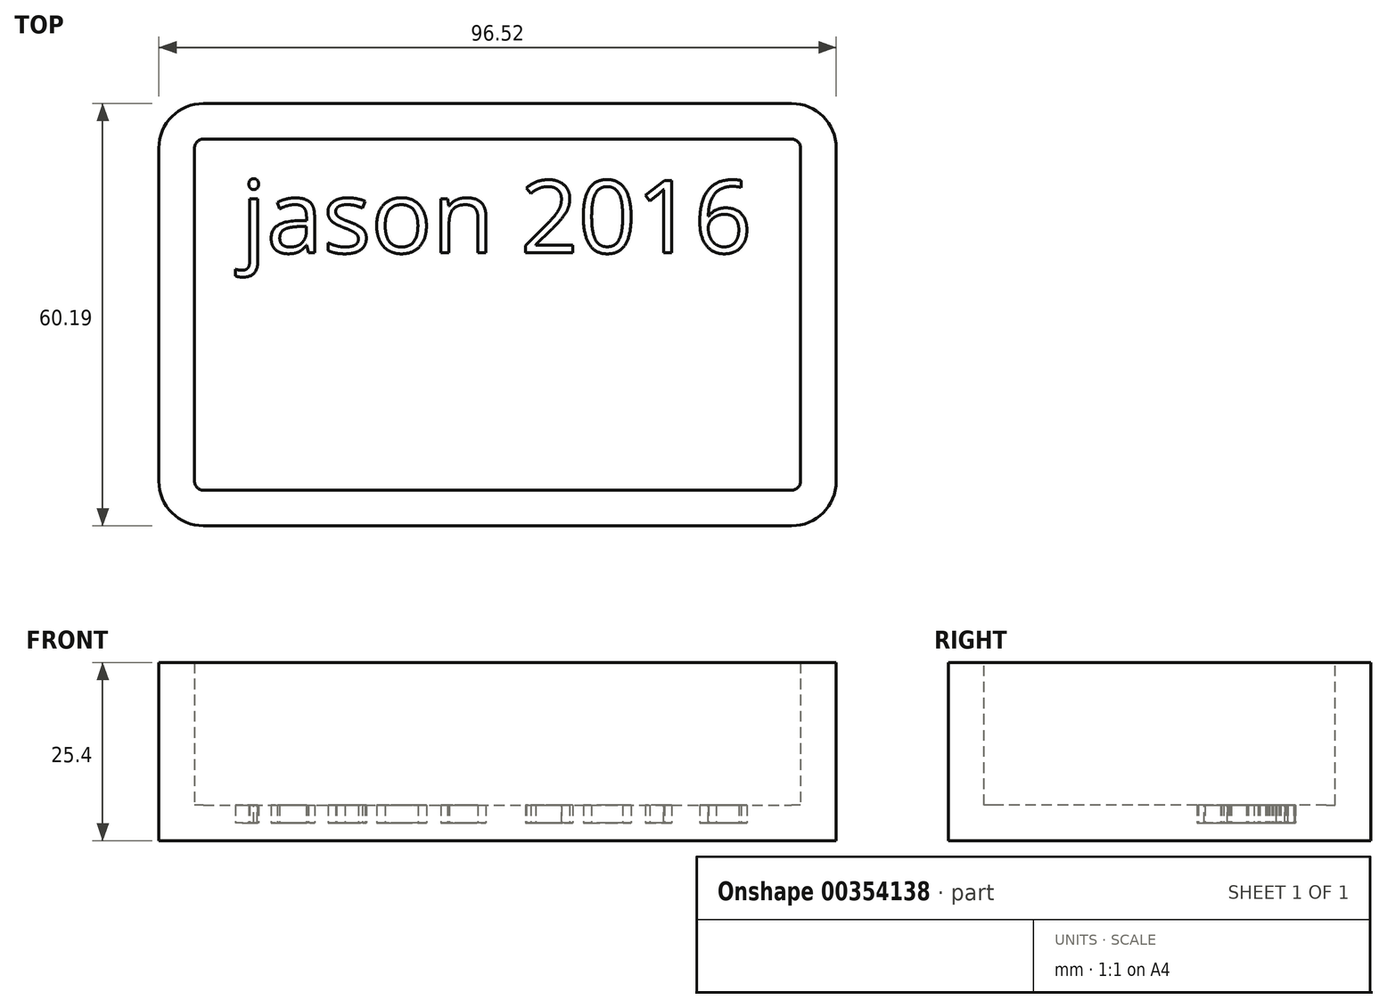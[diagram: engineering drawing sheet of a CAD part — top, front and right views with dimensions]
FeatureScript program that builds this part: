
annotation { "Feature Type Name" : "Feature", "Feature Type Description" : "" }
export const myFeature = defineFeature(function(context is Context, id is Id, definition is map)
    precondition{}
    {
        {
            var Q0;
            Q0=qCreatedBy(makeId("Top.planeOp"),FACE);
            var sketch = newSketch(context, id + "F0", { "sketchPlane" : qUnion([Q0])});
            skLineSegment(sketch, "E0.bottom", {"start": v(-45.53, 28.93) * mm, "end": v(38.3, 28.93) * mm});
            skLineSegment(sketch, "E0.top", {"start": v(-45.53, -31.26) * mm, "end": v(38.3, -31.26) * mm});
            skLineSegment(sketch, "E0.left", {"start": v(-51.88, 22.58) * mm, "end": v(-51.88, -24.91) * mm});
            skLineSegment(sketch, "E0.right", {"start": v(44.64, 22.58) * mm, "end": v(44.64, -24.91) * mm});
            skPoint(sketch, "E1.visualSharp", {"position": v(-51.88, 28.93) * mm});
            skArc(sketch, "E1.filletArc", {"start": v(-45.53, 28.93) * mm, "mid": v(-50.02, 27.07) * mm, "end": v(-51.88, 22.58) * mm});
            skPoint(sketch, "E2.visualSharp", {"position": v(44.64, 28.93) * mm});
            skArc(sketch, "E2.filletArc", {"start": v(44.64, 22.58) * mm, "mid": v(42.78, 27.07) * mm, "end": v(38.3, 28.93) * mm});
            skPoint(sketch, "E3.visualSharp", {"position": v(44.64, -31.26) * mm});
            skArc(sketch, "E3.filletArc", {"start": v(38.3, -31.26) * mm, "mid": v(42.78, -29.4) * mm, "end": v(44.64, -24.91) * mm});
            skPoint(sketch, "E4.visualSharp", {"position": v(-51.88, -31.26) * mm});
            skArc(sketch, "E4.filletArc", {"start": v(-51.88, -24.91) * mm, "mid": v(-50.02, -29.4) * mm, "end": v(-45.53, -31.26) * mm});
            skSolve(sketch);
        }
        {
            var Q0;
            Q0 = qSketchRegion(id + "F0", true);
            extrude(context, id + "F1", {"entities" : qUnion([Q0]), "depth" : 25.4 * mm});
        }
        {
            var Q0;
            Q0=makeQuery(id+"F1.opExtrude","CAP_FACE",FACE,{"disambiguationData":[OSD([sQuery(id+"F0.wireOp",EDGE,"E0.bottom"),sQuery(id+"F0.wireOp",EDGE,"E0.top"),sQuery(id+"F0.wireOp",EDGE,"E0.left"),sQuery(id+"F0.wireOp",EDGE,"E0.right"),sQuery(id+"F0.wireOp",EDGE,"E1.filletArc"),sQuery(id+"F0.wireOp",EDGE,"E2.filletArc"),sQuery(id+"F0.wireOp",EDGE,"E3.filletArc"),sQuery(id+"F0.wireOp",EDGE,"E4.filletArc")])],"isStart":false});
            shell(context, id + "F2", {"entities" : qUnion([Q0]), "thickness" : 5.08 * mm});
        }
        {
            var Q0;
            Q0=qCreatedBy(makeId("Top.planeOp"),FACE);
            var sketch = newSketch(context, id + "F3", { "sketchPlane" : qUnion([Q0])});
            skText(sketch, "E5", { "text": "jason 2016\n", "fontName": "OpenSans-Regular.ttf"});
            const initialGuessF3  = {"E5": [-0.0402, 0.00764, 1, 0, 0.01038]};
            skSetInitialGuess(sketch, initialGuessF3);
            skSolve(sketch);
        }
        {
            var Q0;
            Q0 = qSketchRegion(id + "F3", true);
            extrude(context, id + "F4", {"entities" : qUnion([Q0]), "operationType" : NewBodyOperationType.REMOVE, "depth" : 26.16 * mm, "hasSecondDirection" : true, "secondDirectionOppositeDirection" : false, "secondDirectionDepth" : 2.54 * mm});
        }
    });
